# Revit family: Legrand Coffret Plexo³ 12 modules
name_source: partatom
category: Equipement électrique
revit_build: Autodesk Revit 2018 (Build: 20170223_1515(x64)
units: mm (PartAtom-declared; Revit-internal decimal feet)

## family parameters
Basée sur le plan de construction = Non
Configuration du panneau = Deux colonnes, circuits au sein
Cote de connecteur circulaire = Utiliser le diamètre
Couper avec des vides une fois chargée = Non
Numéro OmniClass = 23.80.30.11.17
Partagée = Non
Point de calcul de pièce = Non
Titre OmniClass = Distribution Boards and Control Panels
Toujours verticalement = Oui
Type d'élément = Tableau de raccordement

## types (16) — shared parameters
Conditions Générale d'Utilisation = https://export.legrand.com
ETIM Class 6.0 = EC000214
Fabricant = Legrand
IK = 09
IP = 65
Image du type = Plexo3_12_modules_001922_pw_153883_pz_0.jpg
Matière = Polystyrène
Polystyrène
RAL = 7046
URL = www.legrand.fr

## per-type parameters (varying)
| type | Bornier N | Bornier T | Coffret 001921 | Coffret 001922 | Coffret 001923 | Coffret 601831 | Coffret 601832 | Coffret 601833 | Coffret 601940 | Coffret 601941 | Coffret 601942 | Coffret 601943 | Coffret 601961 | Coffret 601962 | Coffret 601963 | Coffret 601981 | Coffret 601982 | Coffret 601983 |
| Plexo³ 12 modules 1 rangée 001921 |  | Bornier 5+9 trous | Oui | Non | Non | Non | Non | Non | Non | Non | Non | Non | Non | Non | Non | Non | Non | Non |
| Plexo³ 12 modules 2 rangées 001922 |  | Bornier 5+18 trous | Non | Oui | Non | Non | Non | Non | Non | Non | Non | Non | Non | Non | Non | Non | Non | Non |
| Plexo³ 12 modules 3 rangées 001923 |  | Bornier 5+27 trous | Non | Non | Oui | Non | Non | Non | Non | Non | Non | Non | Non | Non | Non | Non | Non | Non |
| Plexo³ 12 modules 1 rangée 601831 |  | Bornier 5+9 trous | Non | Non | Non | Oui | Non | Non | Non | Non | Non | Non | Non | Non | Non | Non | Non | Non |
| Plexo³ 12 modules 1 rangée 601940 |  |  | Non | Non | Non | Non | Non | Non | Oui | Non | Non | Non | Non | Non | Non | Non | Non | Non |
| Plexo³ 12 modules 1 rangée 601941 | Bornier 8 trous | Bornier 13 trous | Non | Non | Non | Non | Non | Non | Non | Oui | Non | Non | Non | Non | Non | Non | Non | Non |
| Plexo³ 12 modules 1 rangée 601961 |  | Bornier 13 trous | Non | Non | Non | Non | Non | Non | Non | Non | Non | Non | Oui | Non | Non | Non | Non | Non |
| Plexo³ 12 modules 1 rangée 601981 | Bornier 13 trous | Bornier 13 trous | Non | Non | Non | Non | Non | Non | Non | Non | Non | Non | Non | Non | Non | Oui | Non | Non |
| Plexo³ 12 modules 2 rangées 601832 |  | Bornier 5+18 trous | Non | Non | Non | Non | Oui | Non | Non | Non | Non | Non | Non | Non | Non | Non | Non | Non |
| Plexo³ 12 modules 2 rangées 601942 |  |  | Non | Non | Non | Non | Non | Non | Non | Non | Oui | Non | Non | Non | Non | Non | Non | Non |
| Plexo³ 12 modules 2 rangées 601962 |  | Bornier 17 trous | Non | Non | Non | Non | Non | Non | Non | Non | Non | Non | Non | Oui | Non | Non | Non | Non |
| Plexo³ 12 modules 2 rangées 601982 | Bornier 17 trous | Bornier 17 trous | Non | Non | Non | Non | Non | Non | Non | Non | Non | Non | Non | Non | Non | Non | Oui | Non |
| Plexo³ 12 modules 3 rangées 601833 |  | Bornier 5+27 trous | Non | Non | Non | Non | Non | Oui | Non | Non | Non | Non | Non | Non | Non | Non | Non | Non |
| Plexo³ 12 modules 3 rangées 601943 |  |  | Non | Non | Non | Non | Non | Non | Non | Non | Non | Oui | Non | Non | Non | Non | Non | Non |
| Plexo³ 12 modules 3 rangées 601963 |  | Bornier 22 trous | Non | Non | Non | Non | Non | Non | Non | Non | Non | Non | Non | Non | Oui | Non | Non | Non |
| Plexo³ 12 modules 3 rangées 601983 | Bornier 22 trous | Bornier 22 trous | Non | Non | Non | Non | Non | Non | Non | Non | Non | Non | Non | Non | Non | Non | Non | Oui |

note: column(s) folded — value = type name in every type: Description
